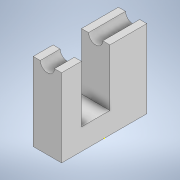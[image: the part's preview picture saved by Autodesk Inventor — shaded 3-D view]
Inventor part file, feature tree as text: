
AUTODESK INVENTOR PART (.ipt)
format: ipt  version: 2021 (Build 250183000, 183)  size: 128,000 bytes
history: native  units: mm
features: sketch x5, extrude x4
ambient origin geometry x8: Origin, YZ Plane, XZ Plane, XY Plane, X Axis, Y Axis, Z Axis, Center Point
bodies: Solid1 (feature_tree)
feature tree (9):
  extrude  "Extrusion1"  Depth=10.0mm
  sketch  "Sketch4"  dims[d2=5.0mm d3=15.0mm]
  extrude  "Extrusion4"  Depth=5.0mm
  extrude  "Extrusion5"  Depth=7.0mm
  extrude  "Extrusion6"  Depth=20.0mm
  sketch  "Sketch1"  dims[d0=30.0mm d1=10.0mm]
  sketch  "Sketch5"  dims[d4=27.5mm d5=0.0mm d12=7.0mm]
  sketch  "Sketch6"  dims[d14=10.0mm d15=20.0mm]
  sketch  "Sketch8"  dims[d16=0.0mm d17=0.0mm d18=5.0mm d19=0.0mm d20=0.0mm d24=3.0mm d26=3.0mm d27=0.0mm d28=19.0mm]
